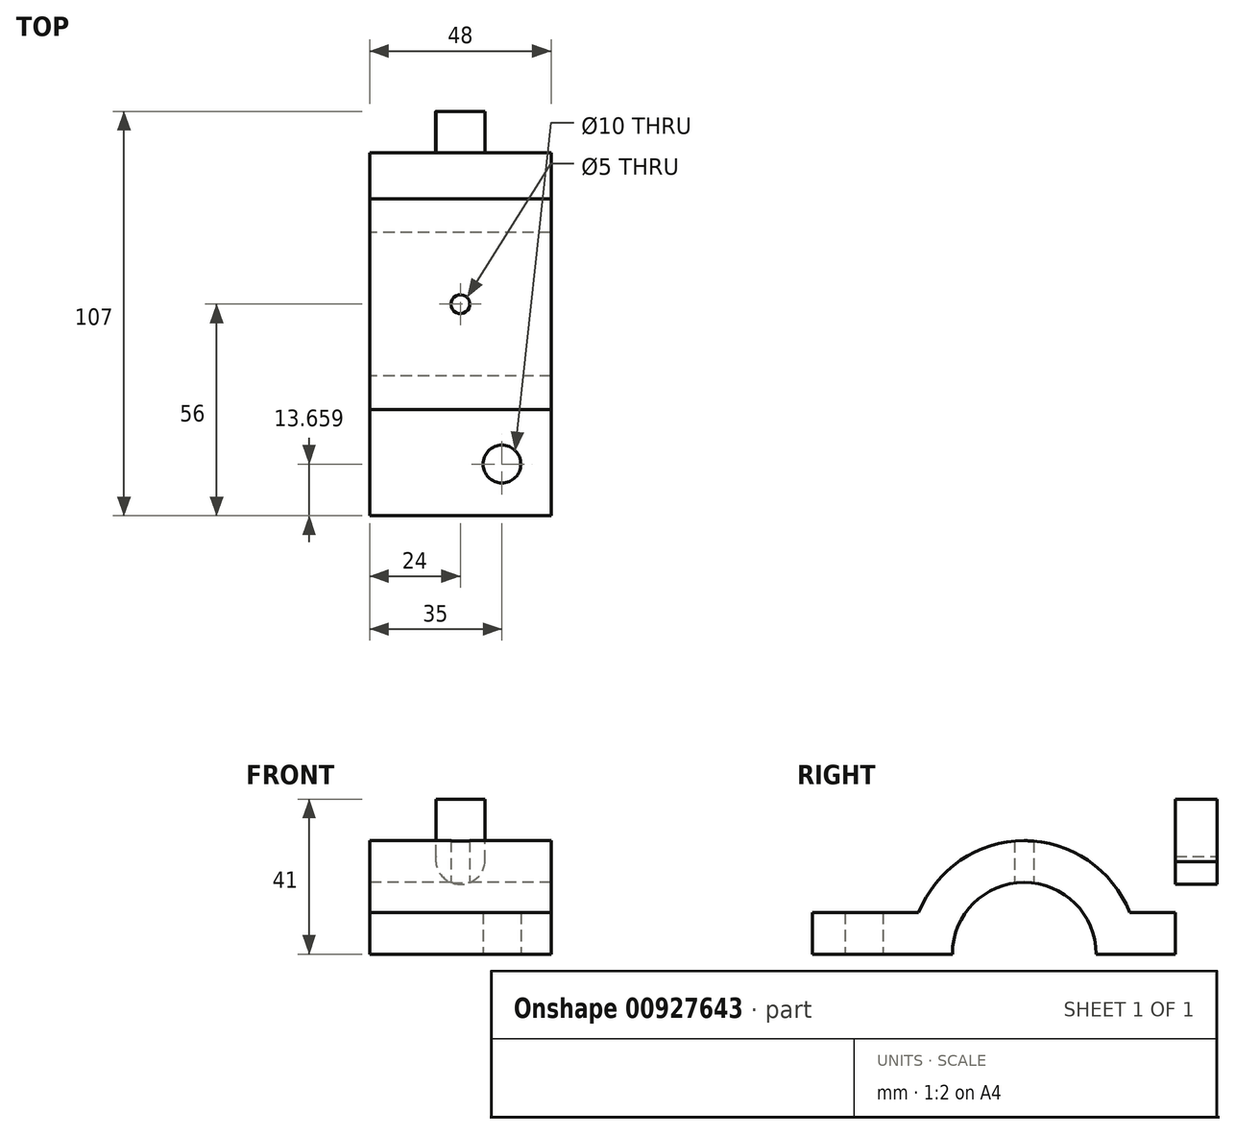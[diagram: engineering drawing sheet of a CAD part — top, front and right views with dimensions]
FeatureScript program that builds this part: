
annotation { "Feature Type Name" : "Feature", "Feature Type Description" : "" }
export const myFeature = defineFeature(function(context is Context, id is Id, definition is map)
    precondition{}
    {
        {
            var Q0;
            Q0=qCreatedBy(makeId("Right.planeOp"),FACE);
            var sketch = newSketch(context, id + "F0", { "sketchPlane" : qUnion([Q0])});
            skCircle(sketch, "E0", {"center": v(0, 0) * mm, "radius": 30 * mm});
            skCircle(sketch, "E1", {"center": v(0, 0) * mm, "radius": 19 * mm});
            skLineSegment(sketch, "E2.bottom", {"start": v(-56, 0) * mm, "end": v(51, 0) * mm});
            skLineSegment(sketch, "E2.top", {"start": v(-56, 11) * mm, "end": v(51, 11) * mm});
            skLineSegment(sketch, "E2.left", {"start": v(-56, 0) * mm, "end": v(-56, 11) * mm});
            skLineSegment(sketch, "E2.right", {"start": v(51, 0) * mm, "end": v(51, 11) * mm});
            skLineSegment(sketch, "E3", {"start": v(0, 0) * mm, "end": v(0, -63.46) * mm, "construction": true});
            skLineSegment(sketch, "E4.bottom", {"start": v(51, 11) * mm, "end": v(40, 11) * mm});
            skLineSegment(sketch, "E4.top", {"start": v(51, 41) * mm, "end": v(40, 41) * mm});
            skLineSegment(sketch, "E4.left", {"start": v(51, 11) * mm, "end": v(51, 41) * mm});
            skLineSegment(sketch, "E4.right", {"start": v(40, 11) * mm, "end": v(40, 41) * mm});
            skSolve(sketch);
        }
        {
            var Q0;
            {var subQ5=sQuery(id+"F0.wireOp",EDGE,"E2.left");Q0=makeQuery(id+"F0.imprint","IMPRINT",FACE,{"disambiguationData":[TD([[makeQuery(id+"F0.imprint","IMPRINT",EDGE,{"derivedFrom":subQ5}),-1.0]])]});}
            var Q1;
            {var subQ0=sQuery(id+"F0.wireOp",EDGE,"E2.top");var subQ1=sQuery(id+"F0.wireOp",EDGE,"E0");var subQ2=makeQuery(id+"F0.imprint","INTERSECT",VERTEX,{"disambiguationData":[OD(1.0)],"derivedFrom":[subQ1,subQ0]});Q1=makeQuery(id+"F0.imprint","IMPRINT",FACE,{"disambiguationData":[TD([[makeQuery(id+"F0.imprint","IMPRINT",EDGE,{"disambiguationData":[TD([[subQ2,-1.0]])],"derivedFrom":subQ1}),1.0]])]});}
            var Q2;
            {var subQ0=sQuery(id+"F0.wireOp",EDGE,"E2.top");var subQ1=sQuery(id+"F0.wireOp",EDGE,"E0");var subQ2=makeQuery(id+"F0.imprint","INTERSECT",VERTEX,{"disambiguationData":[OD(0.0)],"derivedFrom":[subQ1,subQ0]});Q2=makeQuery(id+"F0.imprint","IMPRINT",FACE,{"disambiguationData":[TD([[makeQuery(id+"F0.imprint","IMPRINT",EDGE,{"disambiguationData":[TD([[subQ2,-1.0]])],"derivedFrom":subQ1}),1.0]])]});}
            var Q3;
            {var subQ0=sQuery(id+"F0.wireOp",EDGE,"E2.top");var subQ1=sQuery(id+"F0.wireOp",EDGE,"E0");var subQ2=makeQuery(id+"F0.imprint","INTERSECT",VERTEX,{"disambiguationData":[OD(0.0)],"derivedFrom":[subQ1,subQ0]});Q3=makeQuery(id+"F0.imprint","IMPRINT",FACE,{"disambiguationData":[TD([[makeQuery(id+"F0.imprint","IMPRINT",EDGE,{"disambiguationData":[TD([[subQ2,1.0]])],"derivedFrom":subQ1}),1.0]])]});}
            var Q4;
            {var subQ0=sQuery(id+"F0.wireOp",EDGE,"E2.right");Q4=makeQuery(id+"F0.imprint","IMPRINT",FACE,{"disambiguationData":[TD([[makeQuery(id+"F0.imprint","IMPRINT",EDGE,{"derivedFrom":subQ0}),1.0]])]});}
            var Q5;
            Q5=makeQuery(id+"F0.imprint","IMPRINT",FACE,{"disambiguationData":[TD([[makeQuery(id+"F0.imprint","IMPRINT",EDGE,{"derivedFrom":sQuery(id+"F0.wireOp",EDGE,"E4.top")}),1.0]])]});
            extrude(context, id + "F1", {"entities" : qUnion([Q0, Q1, Q2, Q3, Q4, Q5]), "endBound" : BoundingType.SYMMETRIC, "depth" : 48 * mm, "offsetDistance" : 25 * mm});
        }
        {
            var Q0;
            Q0=makeQuery(id+"F1.opExtrude","SWEPT_FACE",FACE,{"disambiguationData":[OSD([sQuery(id+"F0.wireOp",EDGE,"E2.right"),sQuery(id+"F0.wireOp",EDGE,"E4.left")])]});
            var sketch = newSketch(context, id + "F2", { "sketchPlane" : qUnion([Q0])});
            skCircle(sketch, "E5", {"center": v(0, 25) * mm, "radius": 6.54 * mm});
            skPoint(sketch, "E5.centerSnap0", {"position": v(0, 0) * mm});
            skLineSegment(sketch, "E6", {"start": v(6.48, 24.1) * mm, "end": v(6.48, 41) * mm});
            skLineSegment(sketch, "E7", {"start": v(-6.52, 24.5) * mm, "end": v(-6.52, 41) * mm});
            skSolve(sketch);
        }
        {
            var Q0;
            {var subQ0=sQuery(id+"F2.wireOp",EDGE,"E7");var subQ1=sQuery(id+"F2.wireOp",EDGE,"E5");var subQ2=makeQuery(id+"F2.imprint","INTERSECT",VERTEX,{"disambiguationData":[OD(1.0)],"derivedFrom":[subQ1,subQ0]});Q0=makeQuery(id+"F2.imprint","IMPRINT",FACE,{"disambiguationData":[TD([[makeQuery(id+"F2.imprint","IMPRINT",EDGE,{"disambiguationData":[TD([[subQ2,1.0]])],"derivedFrom":subQ1}),1.0]])]});}
            var Q1;
            {var subQ0=sQuery(id+"F2.wireOp",EDGE,"E7");var subQ1=sQuery(id+"F2.wireOp",EDGE,"E5");var subQ2=makeQuery(id+"F2.imprint","INTERSECT",VERTEX,{"disambiguationData":[OD(1.0)],"derivedFrom":[subQ1,subQ0]});Q1=makeQuery(id+"F2.imprint","IMPRINT",FACE,{"disambiguationData":[TD([[makeQuery(id+"F2.imprint","IMPRINT",EDGE,{"disambiguationData":[TD([[subQ2,1.0]])],"derivedFrom":subQ1}),-1.0]])]});}
            var Q2;
            Q2=makeQuery(id+"F1.opExtrude","SWEPT_FACE",FACE,{"disambiguationData":[OSD([sQuery(id+"F0.wireOp",EDGE,"E4.right")])]});
            extrude(context, id + "F3", {"entities" : qUnion([Q0, Q1]), "operationType" : NewBodyOperationType.REMOVE, "endBound" : BoundingType.UP_TO_SURFACE, "oppositeDirection" : true, "depth" : 11 * mm, "endBoundEntityFace" : qUnion([Q2]), "offsetDistance" : 25 * mm});
        }
        {
            var Q0;
            Q0=qCreatedBy(makeId("Top.planeOp"),FACE);
            var sketch = newSketch(context, id + "F4", { "sketchPlane" : qUnion([Q0])});
            skCircle(sketch, "E8", {"center": v(0, 0) * mm, "radius": 2.5 * mm});
            skCircle(sketch, "E9", {"center": v(11, -42.34) * mm, "radius": 5 * mm});
            skCircle(sketch, "E10.MirrorC", {"center": v(-11, -42.34) * mm, "radius": 5 * mm});
            skSolve(sketch);
        }
        {
            var Q0;
            Q0=makeQuery(id+"F4.imprint","IMPRINT",FACE,{"disambiguationData":[TD([[makeQuery(id+"F4.imprint","IMPRINT",EDGE,{"derivedFrom":sQuery(id+"F4.wireOp",EDGE,"E9")}),1.0]])]});
            var Q1;
            Q1=makeQuery(id+"F4.imprint","IMPRINT",FACE,{"disambiguationData":[TD([[makeQuery(id+"F4.imprint","IMPRINT",EDGE,{"derivedFrom":sQuery(id+"F4.wireOp",EDGE,"E10.MirrorC")}),-1.0]])]});
            var Q2;
            Q2=makeQuery(id+"F4.imprint","IMPRINT",FACE,{"disambiguationData":[TD([[makeQuery(id+"F4.imprint","IMPRINT",EDGE,{"derivedFrom":sQuery(id+"F4.wireOp",EDGE,"E8")}),1.0]])]});
            extrude(context, id + "F5", {"entities" : qUnion([Q0, Q1, Q2]), "operationType" : NewBodyOperationType.REMOVE, "endBound" : BoundingType.THROUGH_ALL, "depth" : 25 * mm, "offsetDistance" : 25 * mm});
        }
    });
